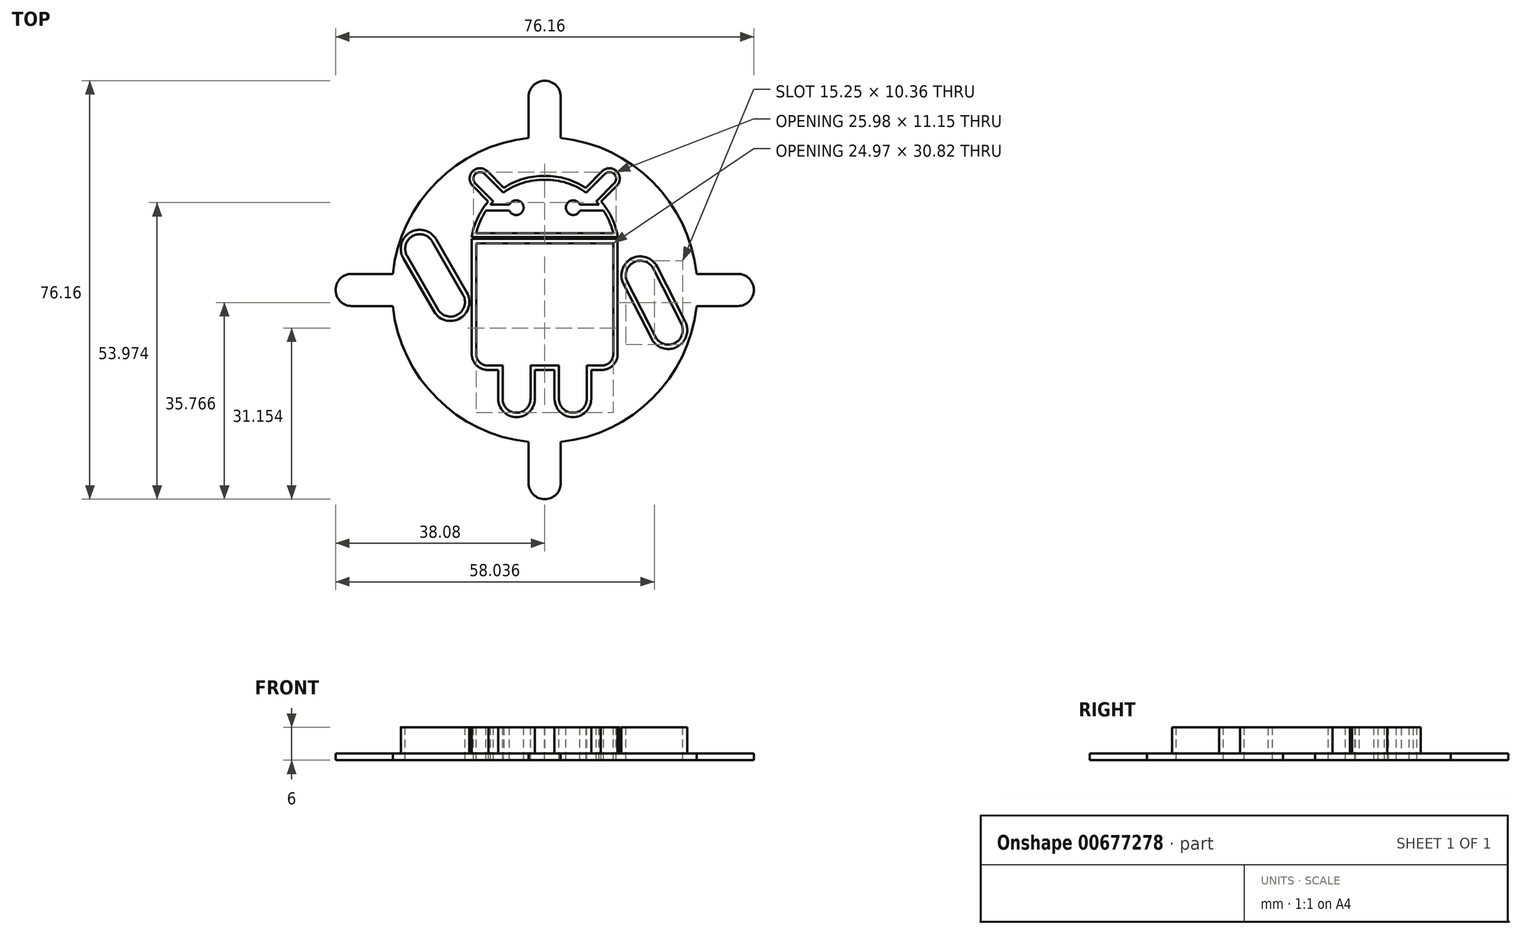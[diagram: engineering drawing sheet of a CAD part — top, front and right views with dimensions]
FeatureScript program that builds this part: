
annotation { "Feature Type Name" : "Feature", "Feature Type Description" : "" }
export const myFeature = defineFeature(function(context is Context, id is Id, definition is map)
    precondition{}
    {
        {
            var Q0;
            Q0=qCreatedBy(makeId("Top.planeOp"),FACE);
            var sketch = newSketch(context, id + "F0", { "sketchPlane" : qUnion([Q0])});
            skCircle(sketch, "E0", {"center": v(0, 0) * mm, "radius": 69.53 * mm});
            skLineSegment(sketch, "E1", {"start": v(-7.31, 69.15) * mm, "end": v(-7.31, 87.88) * mm});
            skPoint(sketch, "E2", {"position": v(0, 69.53) * mm});
            skArc(sketch, "E3", {"start": v(-7.31, 87.88) * mm, "mid": v(-5.17, 93.06) * mm, "end": v(0, 95.2) * mm});
            skLineSegment(sketch, "E4.MirrorCS", {"start": v(7.31, 69.15) * mm, "end": v(7.31, 87.88) * mm});
            skArc(sketch, "E5.MirrorCS", {"start": v(7.31, 87.88) * mm, "mid": v(5.17, 93.06) * mm, "end": v(0, 95.2) * mm});
            skLineSegment(sketch, "E6.1.0", {"start": v(-69.15, -7.31) * mm, "end": v(-87.88, -7.31) * mm});
            skArc(sketch, "E6.1.1", {"start": v(-87.88, -7.31) * mm, "mid": v(-93.06, -5.17) * mm, "end": v(-95.2, 0) * mm});
            skArc(sketch, "E6.1.2", {"start": v(-87.88, 7.31) * mm, "mid": v(-93.06, 5.17) * mm, "end": v(-95.2, 0) * mm});
            skLineSegment(sketch, "E6.1.3", {"start": v(-69.15, 7.31) * mm, "end": v(-87.88, 7.31) * mm});
            skLineSegment(sketch, "E6.2.0", {"start": v(7.31, -69.15) * mm, "end": v(7.31, -87.88) * mm});
            skArc(sketch, "E6.2.1", {"start": v(7.31, -87.88) * mm, "mid": v(5.17, -93.06) * mm, "end": v(0, -95.2) * mm});
            skArc(sketch, "E6.2.2", {"start": v(-7.31, -87.88) * mm, "mid": v(-5.17, -93.06) * mm, "end": v(0, -95.2) * mm});
            skLineSegment(sketch, "E6.2.3", {"start": v(-7.31, -69.15) * mm, "end": v(-7.31, -87.88) * mm});
            skLineSegment(sketch, "E6.3.0", {"start": v(69.15, 7.31) * mm, "end": v(87.88, 7.31) * mm});
            skArc(sketch, "E6.3.1", {"start": v(87.88, 7.31) * mm, "mid": v(93.06, 5.17) * mm, "end": v(95.2, 0) * mm});
            skArc(sketch, "E6.3.2", {"start": v(87.88, -7.31) * mm, "mid": v(93.06, -5.17) * mm, "end": v(95.2, 0) * mm});
            skLineSegment(sketch, "E6.3.3", {"start": v(69.15, -7.31) * mm, "end": v(87.88, -7.31) * mm});
            skSolve(sketch);
        }
        {
            var Q0;
            Q0=qSketchRegion(id+"F0",true);
            extrude(context, id + "F1", {"entities" : qUnion([Q0]), "depth" : 3 * mm, "offsetDistance" : 25 * mm});
        }
        {
            var Q0;
            Q0=makeQuery(id+"F1.opExtrude","CAP_FACE",FACE,{"disambiguationData":[OSD([sQuery(id+"F0.wireOp",EDGE,"E0")])],"isStart":false});
            var sketch = newSketch(context, id + "F2", { "sketchPlane" : qUnion([Q0])});
            skLineSegment(sketch, "E7", {"start": v(-31.2, 21.21) * mm, "end": v(0, 21.21) * mm});
            skLineSegment(sketch, "E8", {"start": v(-31.2, 21.21) * mm, "end": v(-31.2, -29.16) * mm});
            skArc(sketch, "E9", {"start": v(-31.2, -29.16) * mm, "mid": v(-29.55, -32.97) * mm, "end": v(-25.64, -34.37) * mm});
            skLineSegment(sketch, "E10", {"start": v(-25.64, -34.37) * mm, "end": v(-19.17, -34.37) * mm});
            skLineSegment(sketch, "E11", {"start": v(-19.17, -34.37) * mm, "end": v(-19.17, -49.49) * mm});
            skArc(sketch, "E12", {"start": v(-19.17, -49.49) * mm, "mid": v(-12.82, -55.84) * mm, "end": v(-6.47, -49.49) * mm});
            skLineSegment(sketch, "E13", {"start": v(-6.47, -49.49) * mm, "end": v(-6.47, -34.37) * mm});
            skLineSegment(sketch, "E14", {"start": v(-6.47, -34.37) * mm, "end": v(0, -34.37) * mm});
            skLineSegment(sketch, "E15", {"start": v(0, 0) * mm, "end": v(0, 63.34) * mm, "construction": true});
            skPoint(sketch, "E16", {"position": v(0, 21.21) * mm});
            skLineSegment(sketch, "E17", {"start": v(-19.17, -34.37) * mm, "end": v(-6.47, -34.37) * mm, "construction": true});
            skArc(sketch, "E18", {"start": v(0, 50.19) * mm, "mid": v(-9.88, 48.74) * mm, "end": v(-18.82, 44.28) * mm});
            skPoint(sketch, "E18.first.point", {"position": v(-31.2, 25.8) * mm});
            skPoint(sketch, "E18.second.point", {"position": v(0, 50.19) * mm});
            skLineSegment(sketch, "E19", {"start": v(0, 21.21) * mm, "end": v(-31.59, 52.8) * mm, "construction": true});
            skLineSegment(sketch, "E20", {"start": v(-23.36, 40.32) * mm, "end": v(-31.59, 48.55) * mm});
            skLineSegment(sketch, "E21", {"start": v(-31.59, 48.55) * mm, "end": v(-27.34, 52.8) * mm, "construction": true});
            skLineSegment(sketch, "E22", {"start": v(-27.34, 52.8) * mm, "end": v(-18.82, 44.28) * mm});
            skArc(sketch, "E23", {"start": v(-27.34, 52.8) * mm, "mid": v(-31.59, 52.8) * mm, "end": v(-31.59, 48.55) * mm});
            skArc(sketch, "E24", {"start": v(-18.82, 44.28) * mm, "mid": v(-21.19, 42.41) * mm, "end": v(-23.36, 40.32) * mm, "construction": true});
            skArc(sketch, "E25", {"start": v(-23.36, 40.32) * mm, "mid": v(-24.04, 39.6) * mm, "end": v(-24.69, 38.84) * mm});
            skLineSegment(sketch, "E26.bottom", {"start": v(-62.64, 15.46) * mm, "end": v(-51.2, 22.07) * mm, "construction": true});
            skLineSegment(sketch, "E26.top", {"start": v(-48.62, -8.8) * mm, "end": v(-37.19, -2.2) * mm, "construction": true});
            skLineSegment(sketch, "E26.left", {"start": v(-62.64, 15.46) * mm, "end": v(-48.62, -8.8) * mm});
            skLineSegment(sketch, "E26.right", {"start": v(-51.2, 22.07) * mm, "end": v(-37.19, -2.2) * mm});
            skArc(sketch, "E27", {"start": v(-51.2, 22.07) * mm, "mid": v(-60.22, 24.48) * mm, "end": v(-62.64, 15.46) * mm});
            skArc(sketch, "E28", {"start": v(-48.62, -8.8) * mm, "mid": v(-39.6, -11.22) * mm, "end": v(-37.19, -2.2) * mm});
            skPoint(sketch, "E29", {"position": v(-58.02, 31.88) * mm});
            skPoint(sketch, "E30.first.point", {"position": v(-9.61, 37.46) * mm});
            skPoint(sketch, "E30.second.point", {"position": v(-13.05, 40.8) * mm});
            skPoint(sketch, "E30.third.point", {"position": v(-15.18, 34.95) * mm});
            skLineSegment(sketch, "E31", {"start": v(-9.61, 37.46) * mm, "end": v(-25.78, 37.46) * mm, "construction": true});
            skLineSegment(sketch, "E32", {"start": v(-16.01, 38.84) * mm, "end": v(-24.69, 38.84) * mm});
            skLineSegment(sketch, "E33.MirrorCS", {"start": v(-16.01, 36.07) * mm, "end": v(-26.75, 36.07) * mm});
            skPoint(sketch, "E34.orphan", {"position": v(-24.69, 36.07) * mm});
            skArc(sketch, "E35", {"start": v(-24.69, 38.84) * mm, "mid": v(-25.76, 37.48) * mm, "end": v(-26.75, 36.07) * mm, "construction": true});
            skArc(sketch, "E36", {"start": v(-26.75, 36.07) * mm, "mid": v(-29.44, 31.13) * mm, "end": v(-31.2, 25.8) * mm});
            skArc(sketch, "E37", {"start": v(-16.01, 38.84) * mm, "mid": v(-16.3, 37.46) * mm, "end": v(-16.01, 36.07) * mm, "construction": true});
            skArc(sketch, "E38", {"start": v(-16.01, 36.07) * mm, "mid": v(-9.61, 37.46) * mm, "end": v(-16.01, 38.84) * mm});
            skLineSegment(sketch, "E39", {"start": v(-31.2, 25.8) * mm, "end": v(0, 25.8) * mm});
            skArc(sketch, "E40.MirrorCS", {"start": v(0, 50.19) * mm, "mid": v(9.88, 48.74) * mm, "end": v(18.82, 44.28) * mm});
            skLineSegment(sketch, "E41.MirrorCS", {"start": v(27.34, 52.8) * mm, "end": v(18.82, 44.28) * mm});
            skArc(sketch, "E42.MirrorCS", {"start": v(16.01, 38.84) * mm, "mid": v(16.3, 37.46) * mm, "end": v(16.01, 36.07) * mm, "construction": true});
            skArc(sketch, "E43.MirrorCS", {"start": v(23.36, 40.32) * mm, "mid": v(24.04, 39.6) * mm, "end": v(24.69, 38.84) * mm});
            skArc(sketch, "E44.MirrorCS", {"start": v(24.69, 38.84) * mm, "mid": v(25.76, 37.48) * mm, "end": v(26.75, 36.07) * mm, "construction": true});
            skLineSegment(sketch, "E45.MirrorCS", {"start": v(6.47, -34.37) * mm, "end": v(0, -34.37) * mm});
            skLineSegment(sketch, "E46.MirrorCS", {"start": v(31.59, 48.55) * mm, "end": v(27.34, 52.8) * mm, "construction": true});
            skPoint(sketch, "E47.MirrorP", {"position": v(13.05, 40.8) * mm});
            skArc(sketch, "E48.MirrorCS", {"start": v(26.75, 36.07) * mm, "mid": v(29.44, 31.13) * mm, "end": v(31.2, 25.8) * mm});
            skLineSegment(sketch, "E49.MirrorCS", {"start": v(16.01, 36.07) * mm, "end": v(26.75, 36.07) * mm});
            skPoint(sketch, "E50.MirrorP", {"position": v(24.69, 36.07) * mm});
            skLineSegment(sketch, "E51.MirrorCS", {"start": v(23.36, 40.32) * mm, "end": v(31.59, 48.55) * mm});
            skPoint(sketch, "E52.MirrorP", {"position": v(9.61, 37.46) * mm});
            skArc(sketch, "E53.MirrorCS", {"start": v(27.34, 52.8) * mm, "mid": v(31.59, 52.8) * mm, "end": v(31.59, 48.55) * mm});
            skArc(sketch, "E54.MirrorCS", {"start": v(19.17, -49.49) * mm, "mid": v(12.82, -55.84) * mm, "end": v(6.47, -49.49) * mm});
            skLineSegment(sketch, "E55.MirrorCS", {"start": v(25.64, -34.37) * mm, "end": v(19.17, -34.37) * mm});
            skLineSegment(sketch, "E56.MirrorCS", {"start": v(31.2, 21.21) * mm, "end": v(0, 21.21) * mm});
            skLineSegment(sketch, "E57.MirrorCS", {"start": v(6.47, -49.49) * mm, "end": v(6.47, -34.37) * mm});
            skLineSegment(sketch, "E58.MirrorCS", {"start": v(19.17, -34.37) * mm, "end": v(6.47, -34.37) * mm, "construction": true});
            skPoint(sketch, "E59.MirrorP", {"position": v(15.18, 34.95) * mm});
            skPoint(sketch, "E60.MirrorP", {"position": v(31.2, 25.8) * mm});
            skArc(sketch, "E61.MirrorCS", {"start": v(16.01, 36.07) * mm, "mid": v(9.61, 37.46) * mm, "end": v(16.01, 38.84) * mm});
            skLineSegment(sketch, "E62.MirrorCS", {"start": v(9.61, 37.46) * mm, "end": v(25.78, 37.46) * mm, "construction": true});
            skLineSegment(sketch, "E63.MirrorCS", {"start": v(19.17, -34.37) * mm, "end": v(19.17, -49.49) * mm});
            skArc(sketch, "E64.MirrorCS", {"start": v(31.2, -29.16) * mm, "mid": v(29.55, -32.97) * mm, "end": v(25.64, -34.37) * mm});
            skLineSegment(sketch, "E65.MirrorCS", {"start": v(16.01, 38.84) * mm, "end": v(24.69, 38.84) * mm});
            skArc(sketch, "E66.MirrorCS", {"start": v(18.82, 44.28) * mm, "mid": v(21.19, 42.41) * mm, "end": v(23.36, 40.32) * mm, "construction": true});
            skLineSegment(sketch, "E67.MirrorCS", {"start": v(0, 21.21) * mm, "end": v(31.59, 52.8) * mm, "construction": true});
            skLineSegment(sketch, "E68.MirrorCS", {"start": v(31.2, 21.21) * mm, "end": v(31.2, -29.16) * mm});
            skLineSegment(sketch, "E69.MirrorCS", {"start": v(31.2, 25.8) * mm, "end": v(0, 25.8) * mm});
            skLineSegment(sketch, "E70", {"start": v(0, 0) * mm, "end": v(-10.8, 0) * mm, "construction": true});
            skLineSegment(sketch, "E71.MirrorCS", {"start": v(62.14, -15.26) * mm, "end": v(49.4, 9.7) * mm});
            skLineSegment(sketch, "E72.MirrorCS", {"start": v(50.38, -21.27) * mm, "end": v(37.64, 3.7) * mm});
            skArc(sketch, "E73.MirrorCS", {"start": v(62.14, -15.26) * mm, "mid": v(59.27, -24.14) * mm, "end": v(50.38, -21.27) * mm});
            skArc(sketch, "E74.MirrorCS", {"start": v(37.64, 3.7) * mm, "mid": v(40.51, 12.58) * mm, "end": v(49.4, 9.7) * mm});
            skSolve(sketch);
        }
        {
            var Q0;
            Q0=makeQuery(id+"F2.imprint","IMPRINT",FACE,{"disambiguationData":[TD([[makeQuery(id+"F2.imprint","IMPRINT",EDGE,{"derivedFrom":sQuery(id+"F2.wireOp",EDGE,"E26.left")}),1.0]])]});
            var Q1;
            Q1=makeQuery(id+"F2.imprint","IMPRINT",FACE,{"disambiguationData":[TD([[makeQuery(id+"F2.imprint","IMPRINT",EDGE,{"derivedFrom":sQuery(id+"F2.wireOp",EDGE,"E7")}),-1.0]])]});
            var Q2;
            Q2=makeQuery(id+"F2.imprint","IMPRINT",FACE,{"disambiguationData":[TD([[makeQuery(id+"F2.imprint","IMPRINT",EDGE,{"derivedFrom":sQuery(id+"F2.wireOp",EDGE,"4b8b6e5e-5941-414f-89ad-1b3a779556299.MirrorCS")}),-1.0]])]});
            var Q3;
            Q3=makeQuery(id+"F2.imprint","IMPRINT",FACE,{"disambiguationData":[TD([[makeQuery(id+"F2.imprint","IMPRINT",EDGE,{"derivedFrom":sQuery(id+"F2.wireOp",EDGE,"E18")}),1.0]])]});
            var Q4;
            Q4=makeQuery(id+"F2.imprint","IMPRINT",FACE,{"disambiguationData":[TD([[makeQuery(id+"F2.imprint","IMPRINT",EDGE,{"derivedFrom":sQuery(id+"F2.wireOp",EDGE,"E71.MirrorCS")}),1.0]])]});
            extrude(context, id + "F3", {"entities" : qUnion([Q0, Q1, Q2, Q3, Q4]), "operationType" : NewBodyOperationType.REMOVE, "oppositeDirection" : true, "depth" : 25 * mm, "offsetDistance" : 25 * mm});
        }
        {
            var Q0;
            Q0=makeQuery(id+"F1.opExtrude","CAP_FACE",FACE,{"disambiguationData":[OSD([sQuery(id+"F0.wireOp",EDGE,"E0")])],"isStart":false});
            var sketch = newSketch(context, id + "F4", { "sketchPlane" : qUnion([Q0])});
            skLineSegment(sketch, "E75.0", {"start": v(33.2, 23.21) * mm, "end": v(-33.2, 23.21) * mm});
            skLineSegment(sketch, "E75.1", {"start": v(33.2, 23.21) * mm, "end": v(33.2, -29.16) * mm});
            skArc(sketch, "E75.2", {"start": v(33.2, -29.16) * mm, "mid": v(30.95, -34.4) * mm, "end": v(25.58, -36.37) * mm});
            skArc(sketch, "E75.3", {"start": v(-21.17, -49.49) * mm, "mid": v(-12.82, -57.84) * mm, "end": v(-4.47, -49.49) * mm});
            skLineSegment(sketch, "E75.4", {"start": v(-21.17, -36.37) * mm, "end": v(-21.17, -49.49) * mm});
            skLineSegment(sketch, "E75.5", {"start": v(-25.58, -36.37) * mm, "end": v(-21.17, -36.37) * mm});
            skArc(sketch, "E75.6", {"start": v(-33.2, -29.16) * mm, "mid": v(-30.95, -34.4) * mm, "end": v(-25.58, -36.37) * mm});
            skLineSegment(sketch, "E75.7", {"start": v(-4.47, -49.49) * mm, "end": v(-4.47, -36.37) * mm});
            skLineSegment(sketch, "E75.8", {"start": v(-4.47, -36.37) * mm, "end": v(4.47, -36.37) * mm});
            skLineSegment(sketch, "E75.9", {"start": v(4.47, -49.49) * mm, "end": v(4.47, -36.37) * mm});
            skLineSegment(sketch, "E75.10", {"start": v(-33.2, 23.21) * mm, "end": v(-33.2, -29.16) * mm});
            skArc(sketch, "E75.11", {"start": v(21.17, -49.49) * mm, "mid": v(12.82, -57.84) * mm, "end": v(4.47, -49.49) * mm});
            skLineSegment(sketch, "E75.12", {"start": v(21.17, -36.37) * mm, "end": v(21.17, -49.49) * mm});
            skLineSegment(sketch, "E75.13", {"start": v(25.58, -36.37) * mm, "end": v(21.17, -36.37) * mm});
            skArc(sketch, "E76.0", {"start": v(-30.7, 32.46) * mm, "mid": v(-32.27, 28.36) * mm, "end": v(-33.28, 24.1) * mm});
            skArc(sketch, "E76.1", {"start": v(-25.7, 40.26) * mm, "mid": v(-28.48, 36.54) * mm, "end": v(-30.7, 32.46) * mm});
            skArc(sketch, "E76.2", {"start": v(26.14, 54) * mm, "mid": v(32.8, 54) * mm, "end": v(32.8, 47.35) * mm});
            skLineSegment(sketch, "E76.3", {"start": v(25.7, 40.26) * mm, "end": v(32.8, 47.35) * mm});
            skArc(sketch, "E76.4", {"start": v(25.7, 40.26) * mm, "mid": v(28.48, 36.54) * mm, "end": v(30.7, 32.46) * mm});
            skArc(sketch, "E76.5", {"start": v(30.7, 32.46) * mm, "mid": v(32.27, 28.36) * mm, "end": v(33.28, 24.1) * mm});
            skLineSegment(sketch, "E76.6", {"start": v(26.14, 54) * mm, "end": v(18.61, 46.48) * mm});
            skArc(sketch, "E76.7", {"start": v(0, 51.89) * mm, "mid": v(9.7, 50.57) * mm, "end": v(18.61, 46.48) * mm});
            skLineSegment(sketch, "E76.8", {"start": v(-33.28, 24.1) * mm, "end": v(33.28, 24.1) * mm});
            skArc(sketch, "E76.9", {"start": v(0, 51.89) * mm, "mid": v(-9.7, 50.57) * mm, "end": v(-18.61, 46.48) * mm});
            skLineSegment(sketch, "E76.10", {"start": v(-26.14, 54) * mm, "end": v(-18.61, 46.48) * mm});
            skArc(sketch, "E76.11", {"start": v(-26.14, 54) * mm, "mid": v(-32.8, 54) * mm, "end": v(-32.8, 47.35) * mm});
            skLineSegment(sketch, "E76.12", {"start": v(-25.7, 40.26) * mm, "end": v(-32.8, 47.35) * mm});
            skLineSegment(sketch, "E77", {"start": v(-33.2, 23.21) * mm, "end": v(-33.2, 27.37) * mm, "construction": true});
            skArc(sketch, "E78.trimOffspring", {"start": v(-33.2, 6.11) * mm, "mid": v(-33.23, 6.15) * mm, "end": v(-33.26, 6.2) * mm});
            skLineSegment(sketch, "E79.0", {"start": v(-35.46, -1.2) * mm, "end": v(-49.47, 23.07) * mm});
            skArc(sketch, "E79.1", {"start": v(-50.36, -9.8) * mm, "mid": v(-38.6, -12.96) * mm, "end": v(-35.46, -1.2) * mm});
            skLineSegment(sketch, "E79.2", {"start": v(-64.37, 14.46) * mm, "end": v(-50.36, -9.8) * mm});
            skArc(sketch, "E79.3", {"start": v(-49.47, 23.07) * mm, "mid": v(-61.22, 26.22) * mm, "end": v(-64.37, 14.46) * mm});
            skLineSegment(sketch, "E80.0", {"start": v(35.86, 2.78) * mm, "end": v(48.6, -22.18) * mm});
            skArc(sketch, "E80.1", {"start": v(51.18, 10.6) * mm, "mid": v(39.6, 14.36) * mm, "end": v(35.86, 2.78) * mm});
            skLineSegment(sketch, "E80.2", {"start": v(63.93, -14.35) * mm, "end": v(51.18, 10.6) * mm});
            skArc(sketch, "E80.3", {"start": v(48.6, -22.18) * mm, "mid": v(60.18, -25.92) * mm, "end": v(63.93, -14.35) * mm});
            skLineSegment(sketch, "E81.0.0", {"start": v(-37.19, -2.2) * mm, "end": v(-51.2, 22.07) * mm});
            skArc(sketch, "E81.0.1", {"start": v(-51.2, 22.07) * mm, "mid": v(-60.22, 24.48) * mm, "end": v(-62.64, 15.46) * mm});
            skLineSegment(sketch, "E81.0.2", {"start": v(-62.64, 15.46) * mm, "end": v(-48.62, -8.8) * mm});
            skArc(sketch, "E81.0.3", {"start": v(-48.62, -8.8) * mm, "mid": v(-39.6, -11.22) * mm, "end": v(-37.19, -2.2) * mm});
            skLineSegment(sketch, "E82.0.0", {"start": v(37.64, 3.7) * mm, "end": v(50.38, -21.27) * mm});
            skArc(sketch, "E82.0.1", {"start": v(50.38, -21.27) * mm, "mid": v(59.27, -24.14) * mm, "end": v(62.14, -15.26) * mm});
            skLineSegment(sketch, "E82.0.2", {"start": v(62.14, -15.26) * mm, "end": v(49.4, 9.7) * mm});
            skArc(sketch, "E82.0.3", {"start": v(49.4, 9.7) * mm, "mid": v(40.51, 12.58) * mm, "end": v(37.64, 3.7) * mm});
            skSolve(sketch);
        }
        {
            assignVariable(context, id + "F5", {"name" : "extrude", "anyValue" : 12 * mm});
        }
        {
            var Q0;
            Q0=makeQuery(id+"F4.imprint","IMPRINT",FACE,{"disambiguationData":[TD([[makeQuery(id+"F4.imprint","IMPRINT",EDGE,{"derivedFrom":sQuery(id+"F4.wireOp",EDGE,"E80.0")}),1.0]])]});
            var Q1;
            Q1=makeQuery(id+"F4.imprint","IMPRINT",FACE,{"disambiguationData":[TD([[makeQuery(id+"F4.imprint","IMPRINT",EDGE,{"derivedFrom":sQuery(id+"F4.wireOp",EDGE,"E79.0")}),1.0]])]});
            extrude(context, id + "F6", {"entities" : qUnion([Q0, Q1]), "operationType" : NewBodyOperationType.ADD, "depth" : getVariable(context, 'extrude'), "offsetDistance" : 25 * mm});
        }
        {
            var Q0;
            {var subQ3=sQuery(id+"F4.wireOp",EDGE,"E75.0");Q0=makeQuery(id+"F4.imprint","IMPRINT",FACE,{"disambiguationData":[TD([[makeQuery(id+"F4.imprint","IMPRINT",EDGE,{"derivedFrom":subQ3}),1.0]])]});}
            var Q1;
            Q1=makeQuery(id+"F4.imprint","IMPRINT",FACE,{"disambiguationData":[TD([[makeQuery(id+"F4.imprint","IMPRINT",EDGE,{"derivedFrom":sQuery(id+"F4.wireOp",EDGE,"E76.0")}),1.0]])]});
            extrude(context, id + "F7", {"entities" : qUnion([Q0, Q1]), "operationType" : NewBodyOperationType.ADD, "depth" : getVariable(context, 'extrude'), "offsetDistance" : 25 * mm});
        }
        {
            var Q0;
            Q0=makeQuery(id+"F1.opExtrude","SWEPT_BODY",BODY,{"disambiguationData":[OSD([sQuery(id+"F0.wireOp",EDGE,"E0"),sQuery(id+"F0.wireOp",EDGE,"E1"),sQuery(id+"F0.wireOp",EDGE,"E3"),sQuery(id+"F0.wireOp",EDGE,"E4.MirrorCS"),sQuery(id+"F0.wireOp",EDGE,"E5.MirrorCS"),sQuery(id+"F0.wireOp",EDGE,"E6.1.0"),sQuery(id+"F0.wireOp",EDGE,"E6.1.1"),sQuery(id+"F0.wireOp",EDGE,"E6.1.2"),sQuery(id+"F0.wireOp",EDGE,"E6.1.3"),sQuery(id+"F0.wireOp",EDGE,"E6.2.0"),sQuery(id+"F0.wireOp",EDGE,"E6.2.1"),sQuery(id+"F0.wireOp",EDGE,"E6.2.2"),sQuery(id+"F0.wireOp",EDGE,"E6.2.3"),sQuery(id+"F0.wireOp",EDGE,"E6.3.0"),sQuery(id+"F0.wireOp",EDGE,"E6.3.1"),sQuery(id+"F0.wireOp",EDGE,"E6.3.2"),sQuery(id+"F0.wireOp",EDGE,"E6.3.3")])]});
            var Q1;
            Q1=qCreatedBy(makeId("Origin.pointOp"),VERTEX);
            transform(context, id + "F8", {"entities" : qUnion([Q0]), "transformType" : TransformType.SCALE_UNIFORMLY, "scale" : 0.5, "scalePoint" : qUnion([Q1]), "makeCopy" : false});
        }
        {
            var Q0;
            Q0=makeQuery(id+"F1.opExtrude","SWEPT_BODY",BODY,{"disambiguationData":[OSD([sQuery(id+"F0.wireOp",EDGE,"E0")])]});
            var Q1;
            Q1=qCreatedBy(makeId("Origin.pointOp"),VERTEX);
            transform(context, id + "F9", {"entities" : qUnion([Q0]), "transformType" : TransformType.SCALE_UNIFORMLY, "scale" : 0.8, "scalePoint" : qUnion([Q1]), "makeCopy" : false});
        }
    });
